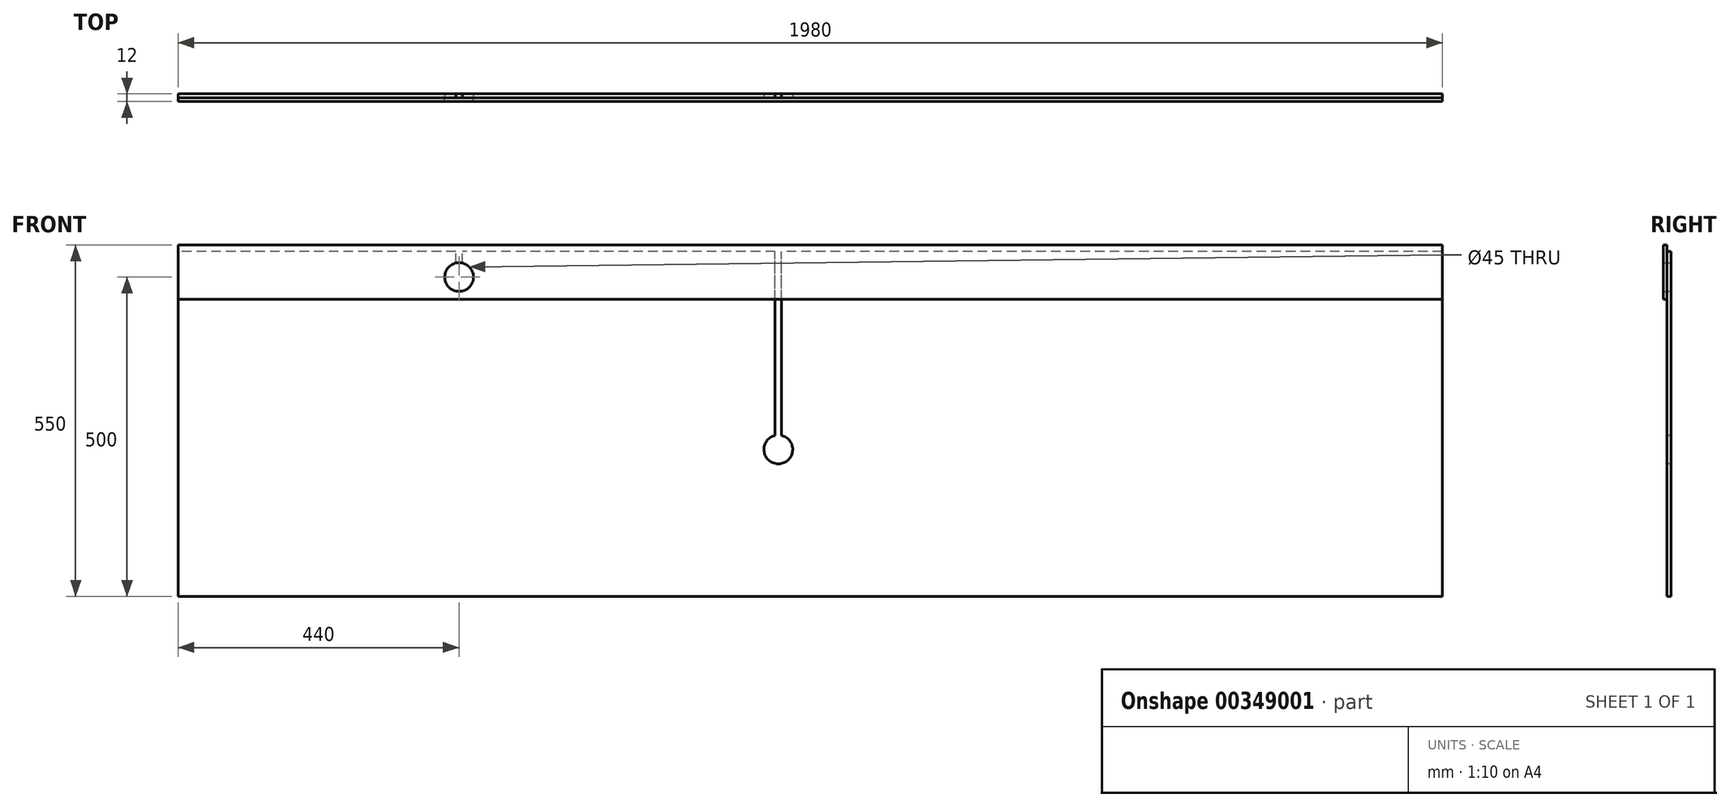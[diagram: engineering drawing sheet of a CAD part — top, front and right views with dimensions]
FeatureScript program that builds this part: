
annotation { "Feature Type Name" : "Feature", "Feature Type Description" : "" }
export const myFeature = defineFeature(function(context is Context, id is Id, definition is map)
    precondition{}
    {
        {
            var Q0;
            Q0=qCreatedBy(makeId("Front.planeOp"),FACE);
            var sketch = newSketch(context, id + "F0", { "sketchPlane" : qUnion([Q0])});
            skLineSegment(sketch, "E0.bottom", {"start": v(990, 0) * mm, "end": v(-990, 0) * mm});
            skLineSegment(sketch, "E0.top", {"start": v(990, 550) * mm, "end": v(-990, 550) * mm});
            skLineSegment(sketch, "E0.left", {"start": v(990, 0) * mm, "end": v(990, 550) * mm});
            skLineSegment(sketch, "E0.right", {"start": v(-990, 0) * mm, "end": v(-990, 550) * mm});
            skPoint(sketch, "E0.middle", {"position": v(0, 275) * mm});
            skSolve(sketch);
        }
        {
            var Q0;
            Q0 = qSketchRegion(id + "F0", true);
            extrude(context, id + "F1", {"entities" : qUnion([Q0]), "depth" : 6 * mm});
        }
        {
            var Q0;
            Q0=makeQuery(id+"F1.opExtrude","CAP_FACE",FACE,{"disambiguationData":[OSD([sQuery(id+"F0.wireOp",EDGE,"E0.bottom"),sQuery(id+"F0.wireOp",EDGE,"E0.top"),sQuery(id+"F0.wireOp",EDGE,"E0.left"),sQuery(id+"F0.wireOp",EDGE,"E0.right")])],"isStart":false});
            var sketch = newSketch(context, id + "F2", { "sketchPlane" : qUnion([Q0])});
            skLineSegment(sketch, "E1.bottom", {"start": v(-990, 550) * mm, "end": v(990, 550) * mm});
            skLineSegment(sketch, "E1.top", {"start": v(-990, 465) * mm, "end": v(990, 465) * mm});
            skLineSegment(sketch, "E1.left", {"start": v(-990, 550) * mm, "end": v(-990, 465) * mm});
            skLineSegment(sketch, "E1.right", {"start": v(990, 550) * mm, "end": v(990, 465) * mm});
            skSolve(sketch);
        }
        {
            var Q0;
            Q0 = qSketchRegion(id + "F2", true);
            extrude(context, id + "F3", {"entities" : qUnion([Q0]), "depth" : 6 * mm});
        }
        {
            var Q0;
            Q0=makeQuery(id+"F1.opExtrude","CAP_FACE",FACE,{"disambiguationData":[OSD([sQuery(id+"F0.wireOp",EDGE,"E0.bottom"),sQuery(id+"F0.wireOp",EDGE,"E0.top"),sQuery(id+"F0.wireOp",EDGE,"E0.left"),sQuery(id+"F0.wireOp",EDGE,"E0.right")])],"isStart":false});
            var sketch = newSketch(context, id + "F4", { "sketchPlane" : qUnion([Q0])});
            skCircle(sketch, "E2", {"center": v(-50, 230) * mm, "radius": 22.5 * mm});
            skCircle(sketch, "E3", {"center": v(-550, 500) * mm, "radius": 22.5 * mm});
            skSolve(sketch);
        }
        {
            var Q0;
            Q0 = qSketchRegion(id + "F4", true);
            extrude(context, id + "F5", {"entities" : qUnion([Q0]), "operationType" : NewBodyOperationType.REMOVE, "endBound" : BoundingType.THROUGH_ALL, "oppositeDirection" : true, "depth" : 25 * mm});
        }
        {
            var Q0;
            Q0=makeQuery(id+"F1.opExtrude","CAP_FACE",FACE,{"disambiguationData":[OSD([sQuery(id+"F0.wireOp",EDGE,"E0.bottom"),sQuery(id+"F0.wireOp",EDGE,"E0.top"),sQuery(id+"F0.wireOp",EDGE,"E0.left"),sQuery(id+"F0.wireOp",EDGE,"E0.right")])],"isStart":false});
            var sketch = newSketch(context, id + "F6", { "sketchPlane" : qUnion([Q0])});
            skLineSegment(sketch, "E4", {"start": v(-50, 230) * mm, "end": v(-50, 402.64) * mm, "construction": true});
            skLineSegment(sketch, "E5.bottom", {"start": v(-45, 230) * mm, "end": v(-55, 230) * mm});
            skLineSegment(sketch, "E5.top", {"start": v(-45, 550) * mm, "end": v(-55, 550) * mm});
            skLineSegment(sketch, "E5.left", {"start": v(-45, 230) * mm, "end": v(-45, 550) * mm});
            skLineSegment(sketch, "E5.right", {"start": v(-55, 230) * mm, "end": v(-55, 550) * mm});
            skPoint(sketch, "E5.middle", {"position": v(-50, 390) * mm});
            skLineSegment(sketch, "E6", {"start": v(-550, 500) * mm, "end": v(-550, 812.58) * mm, "construction": true});
            skLineSegment(sketch, "E7.bottom", {"start": v(-555, 500) * mm, "end": v(-545, 500) * mm});
            skLineSegment(sketch, "E7.top", {"start": v(-555, 550) * mm, "end": v(-545, 550) * mm});
            skLineSegment(sketch, "E7.left", {"start": v(-555, 500) * mm, "end": v(-555, 550) * mm});
            skLineSegment(sketch, "E7.right", {"start": v(-545, 500) * mm, "end": v(-545, 550) * mm});
            skPoint(sketch, "E7.middle", {"position": v(-550, 525) * mm});
            skSolve(sketch);
        }
        {
            var Q0;
            Q0 = qSketchRegion(id + "F6", true);
            extrude(context, id + "F7", {"entities" : qUnion([Q0]), "operationType" : NewBodyOperationType.REMOVE, "endBound" : BoundingType.THROUGH_ALL, "oppositeDirection" : true, "depth" : 25 * mm});
        }
        {
            var Q0;
            Q0=makeQuery(id+"F1.opExtrude","CAP_FACE",FACE,{"disambiguationData":[OSD([sQuery(id+"F0.wireOp",EDGE,"E0.bottom"),sQuery(id+"F0.wireOp",EDGE,"E0.top"),sQuery(id+"F0.wireOp",EDGE,"E0.left"),sQuery(id+"F0.wireOp",EDGE,"E0.right")])],"isStart":false});
            var sketch = newSketch(context, id + "F8", { "sketchPlane" : qUnion([Q0])});
            skLineSegment(sketch, "E8.bottom", {"start": v(990, 550) * mm, "end": v(-990, 550) * mm});
            skLineSegment(sketch, "E8.top", {"start": v(990, 540) * mm, "end": v(-990, 540) * mm});
            skLineSegment(sketch, "E8.left", {"start": v(990, 550) * mm, "end": v(990, 540) * mm});
            skLineSegment(sketch, "E8.right", {"start": v(-990, 550) * mm, "end": v(-990, 540) * mm});
            skPoint(sketch, "E8.middle", {"position": v(0, 545) * mm});
            skSolve(sketch);
        }
        {
            var Q0;
            Q0 = qSketchRegion(id + "F8", true);
            extrude(context, id + "F9", {"entities" : qUnion([Q0]), "operationType" : NewBodyOperationType.REMOVE, "endBound" : BoundingType.THROUGH_ALL, "oppositeDirection" : true, "depth" : 25 * mm});
        }
        {
            var Q0;
            Q0=makeQuery(id+"F3.opExtrude","CAP_FACE",FACE,{"disambiguationData":[OSD([sQuery(id+"F2.wireOp",EDGE,"E1.bottom"),sQuery(id+"F2.wireOp",EDGE,"E1.top"),sQuery(id+"F2.wireOp",EDGE,"E1.left"),sQuery(id+"F2.wireOp",EDGE,"E1.right")])],"isStart":true});
            var sketch = newSketch(context, id + "F10", { "sketchPlane" : qUnion([Q0])});
            skCircle(sketch, "E9", {"center": v(550, 500) * mm, "radius": 22.5 * mm});
            skSolve(sketch);
        }
        {
            var Q0;
            Q0 = qSketchRegion(id + "F10", true);
            extrude(context, id + "F11", {"entities" : qUnion([Q0]), "operationType" : NewBodyOperationType.REMOVE, "oppositeDirection" : true, "depth" : 25 * mm});
        }
    });
